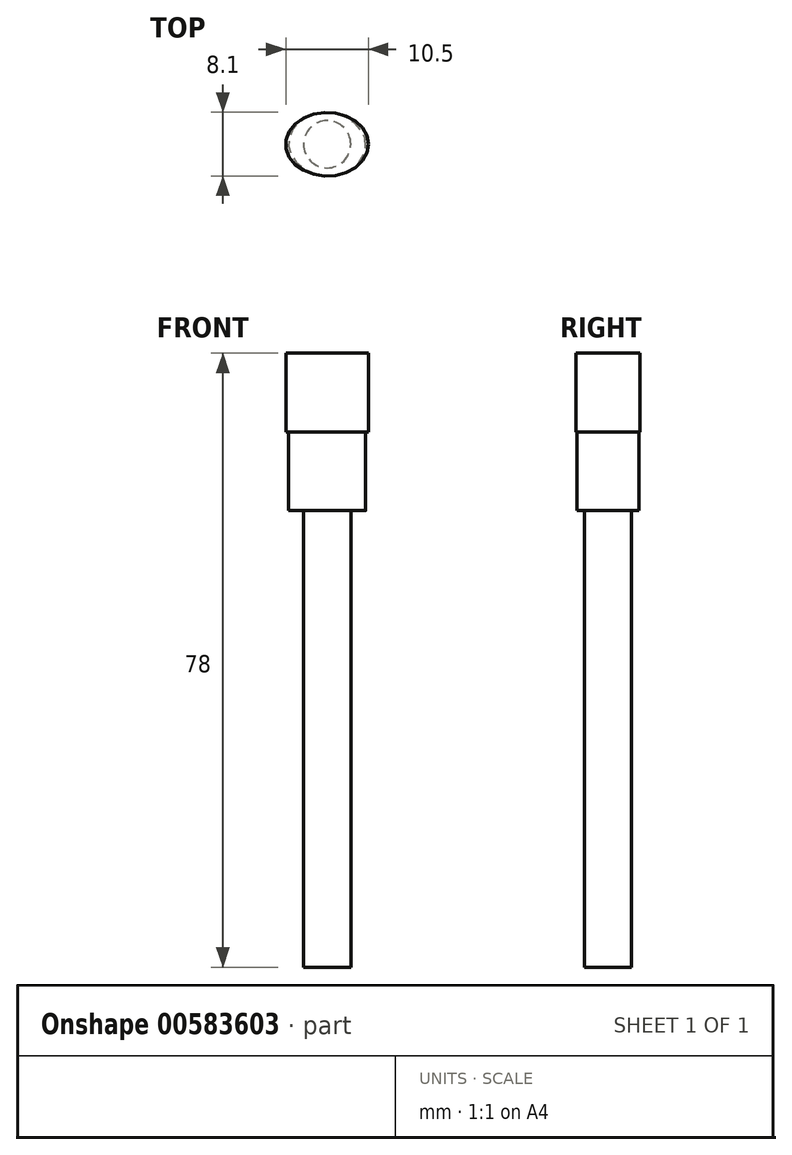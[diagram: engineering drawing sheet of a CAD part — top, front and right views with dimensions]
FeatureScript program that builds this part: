
annotation { "Feature Type Name" : "Feature", "Feature Type Description" : "" }
export const myFeature = defineFeature(function(context is Context, id is Id, definition is map)
    precondition{}
    {
        {
            var Q0;
            Q0=qCreatedBy(makeId("Top.planeOp"),FACE);
            var sketch = newSketch(context, id + "F0", { "sketchPlane" : qUnion([Q0])});
            skEllipse(sketch, "E0", {"center": v(0, 0) * mm, "majorRadius": 4.9 * mm, "minorRadius": 3.95 * mm, "majorAxis": v(1, -0.06)});
            skSolve(sketch);
        }
        {
            var Q0;
            Q0=makeQuery(id+"F0.imprint","IMPRINT",FACE,{"disambiguationData":[TD([[makeQuery(id+"F0.imprint","IMPRINT",EDGE,{"derivedFrom":sQuery(id+"F0.wireOp",EDGE,"E0")}),1.0]])]});
            extrude(context, id + "F1", {"entities" : qUnion([Q0]), "depth" : 10 * mm, "offsetDistance" : 25 * mm});
        }
        {
            var Q0;
            Q0=makeQuery(id+"F1.opExtrude","CAP_FACE",FACE,{"disambiguationData":[OSD([sQuery(id+"F0.wireOp",EDGE,"E0")])],"isStart":false});
            var sketch = newSketch(context, id + "F2", { "sketchPlane" : qUnion([Q0])});
            skEllipse(sketch, "E1", {"center": v(0, 0) * mm, "majorRadius": 5.25 * mm, "minorRadius": 4.05 * mm, "majorAxis": v(1, 0)});
            skSolve(sketch);
        }
        {
            var Q0;
            Q0 = qSketchRegion(id + "F2", true);
            extrude(context, id + "F3", {"entities" : qUnion([Q0]), "operationType" : NewBodyOperationType.ADD, "depth" : 10 * mm, "offsetDistance" : 25 * mm});
        }
        {
            var Q0;
            Q0=makeQuery(id+"F1.opExtrude","CAP_FACE",FACE,{"disambiguationData":[OSD([sQuery(id+"F0.wireOp",EDGE,"E0")])],"isStart":true});
            var sketch = newSketch(context, id + "F4", { "sketchPlane" : qUnion([Q0])});
            skCircle(sketch, "E2", {"center": v(0, 0) * mm, "radius": 3 * mm});
            skSolve(sketch);
        }
        {
            var Q0;
            Q0=makeQuery(id+"F4.imprint","IMPRINT",FACE,{"disambiguationData":[TD([[makeQuery(id+"F4.imprint","IMPRINT",EDGE,{"derivedFrom":sQuery(id+"F4.wireOp",EDGE,"E2")}),1.0]])]});
            extrude(context, id + "F5", {"entities" : qUnion([Q0]), "operationType" : NewBodyOperationType.ADD, "depth" : 58 * mm, "offsetDistance" : 25 * mm});
        }
    });
